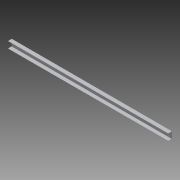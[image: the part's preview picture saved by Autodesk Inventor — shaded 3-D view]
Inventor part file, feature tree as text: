
AUTODESK INVENTOR PART (.ipt)
format: ipt  version: 2013 (Build 170138000, 138)  size: 80,384 bytes
history: native  units: in
note: dims shown in document units (in); Inventor stores cm internally (conversion verified against a paired STEP export)
features: other x2, extrude x1, sketch x1
ambient origin geometry x8: Origin, YZ Plane, XZ Plane, XY Plane, X Axis, Y Axis, Z Axis, Center Point
bodies: Solid1 (feature_tree)
feature tree (4):
  other  "Table"
  other  "Part1-01"
  extrude  "Extrusion1"  Depth=2.25in
  sketch  "Sketch1"  dims[d0=4.0in d1=2.25in d2=0.125in d4=0.0in]
